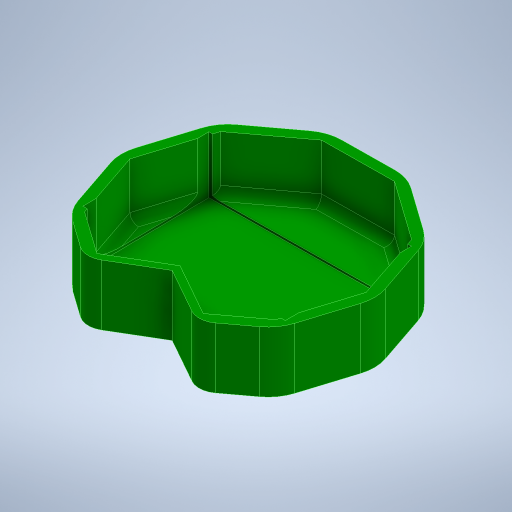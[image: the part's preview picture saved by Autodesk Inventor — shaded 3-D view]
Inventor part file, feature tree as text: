
AUTODESK INVENTOR PART (.ipt)
format: ipt  version: 2024 (Build 280153000, 153)  size: 371,200 bytes
history: native  units: in
note: dims shown in document units (in); Inventor stores cm internally (conversion verified against a paired STEP export)
features: extrude x3, fillet x3, sketch x2
ambient origin geometry x8: Origin, YZ Plane, XZ Plane, XY Plane, X Axis, Y Axis, Z Axis, Center Point
bodies: Body1 (feature_tree)
feature tree (8):
  sketch  "Sketch3"  dims[d22=2.4803in d23=0.6299in]
  extrude  "Extrusion3"  Depth=0.6299in
  extrude  "Extrusion4"  Depth=0.0669in
  extrude  "Extrusion5"  TaperAngle=120.0deg  [1 undecoded]
  fillet  "Fillet1"  Radius=0.0591in
  fillet  "Fillet2"  Radius=0.5906in
  fillet  "Fillet5"  Radius=0.5in
  sketch  "Sketch4"  dims[d24=0.0984in d25=0.0669in d26=120.0deg d27=0.0591in d28=0.0in d29=0.5906in d30=0.0in d31=0.5in d32=1.8898in d33=1.1811in d34=0.5315in d35=0.0in d36=0.0295in d37=0.3937in d38=0.0787in d40=0.0236in d41=0.0in d46=0.1969in]
note: 1 required parameter value undecoded (feature->parameter linkage not recoverable at this tier; creation-order binding heuristic only, values carry confidence <= 0.55)
